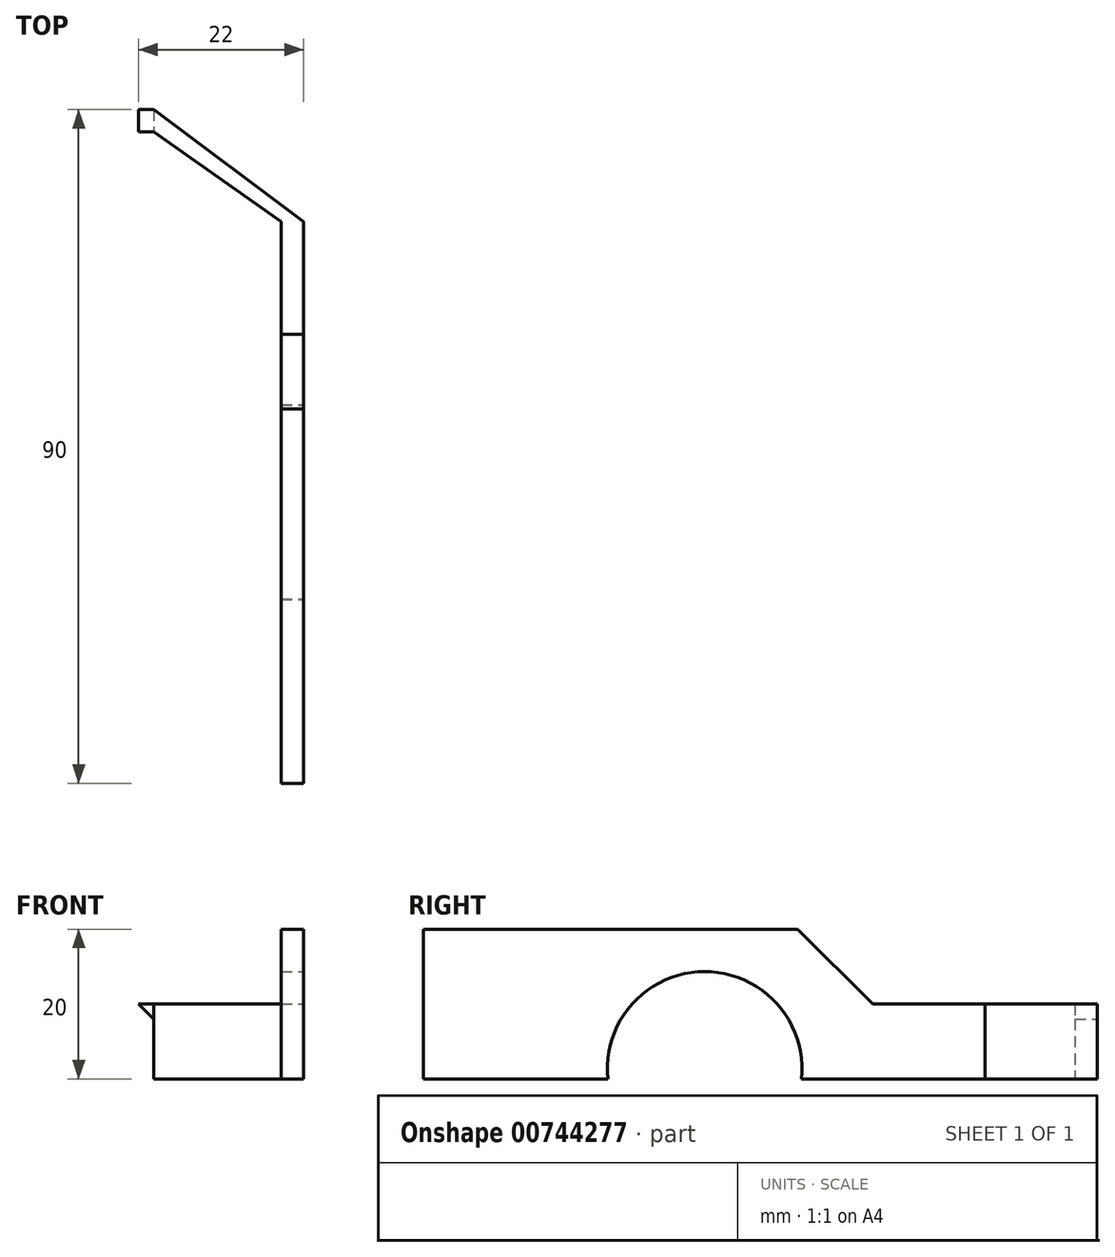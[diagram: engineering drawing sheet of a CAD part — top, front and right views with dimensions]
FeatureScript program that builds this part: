
annotation { "Feature Type Name" : "Feature", "Feature Type Description" : "" }
export const myFeature = defineFeature(function(context is Context, id is Id, definition is map)
    precondition{}
    {
        {
            var Q0;
            Q0=qCreatedBy(makeId("Top.planeOp"),FACE);
            var sketch = newSketch(context, id + "F0", { "sketchPlane" : qUnion([Q0])});
            skLineSegment(sketch, "E0", {"start": v(0, 0) * mm, "end": v(0, -3) * mm});
            skLineSegment(sketch, "E1", {"start": v(0, -3) * mm, "end": v(17, -15) * mm});
            skLineSegment(sketch, "E2", {"start": v(17, -15) * mm, "end": v(17, -90) * mm});
            skLineSegment(sketch, "E3", {"start": v(17, -90) * mm, "end": v(20, -90) * mm});
            skLineSegment(sketch, "E4", {"start": v(20, -90) * mm, "end": v(20, -15) * mm});
            skLineSegment(sketch, "E5", {"start": v(20, -15) * mm, "end": v(0, 0) * mm});
            skSolve(sketch);
        }
        {
            var Q0;
            Q0 = qSketchRegion(id + "F0", true);
            extrude(context, id + "F1", {"entities" : qUnion([Q0]), "depth" : 10 * mm, "offsetDistance" : 25 * mm});
        }
        {
            var Q0;
            Q0=qCreatedBy(makeId("Front.planeOp"),FACE);
            var sketch = newSketch(context, id + "F2", { "sketchPlane" : qUnion([Q0])});
            skLineSegment(sketch, "E6", {"start": v(0, 10) * mm, "end": v(-2, 10) * mm});
            skLineSegment(sketch, "E7", {"start": v(-2, 10) * mm, "end": v(0, 8) * mm});
            skLineSegment(sketch, "E8", {"start": v(0, 8) * mm, "end": v(0, 10) * mm});
            skSolve(sketch);
        }
        {
            var Q0;
            Q0 = qSketchRegion(id + "F2", true);
            extrude(context, id + "F3", {"entities" : qUnion([Q0]), "operationType" : NewBodyOperationType.ADD, "depth" : 3 * mm, "offsetDistance" : 25 * mm});
        }
        {
            var Q0;
            Q0=makeQuery(id+"F3.boolean.opBoolean","MERGE",FACE,{"derivedFrom":[makeQuery(id+"F1.opExtrude","CAP_FACE",FACE,{"disambiguationData":[OSD([sQuery(id+"F0.wireOp",EDGE,"E0"),sQuery(id+"F0.wireOp",EDGE,"E1"),sQuery(id+"F0.wireOp",EDGE,"E2"),sQuery(id+"F0.wireOp",EDGE,"E3"),sQuery(id+"F0.wireOp",EDGE,"E4"),sQuery(id+"F0.wireOp",EDGE,"E5")])],"isStart":false}),makeQuery(id+"F3.opExtrude","SWEPT_FACE",FACE,{"disambiguationData":[OSD([sQuery(id+"F2.wireOp",EDGE,"E6")])]})]});
            var sketch = newSketch(context, id + "F4", { "sketchPlane" : qUnion([Q0])});
            skLineSegment(sketch, "E9.bottom", {"start": v(17, -30) * mm, "end": v(20, -30) * mm});
            skLineSegment(sketch, "E9.top", {"start": v(17, -90) * mm, "end": v(20, -90) * mm});
            skLineSegment(sketch, "E9.left", {"start": v(17, -30) * mm, "end": v(17, -90) * mm});
            skLineSegment(sketch, "E9.right", {"start": v(20, -30) * mm, "end": v(20, -90) * mm});
            skSolve(sketch);
        }
        {
            var Q0;
            Q0 = qSketchRegion(id + "F4", true);
            extrude(context, id + "F5", {"entities" : qUnion([Q0]), "operationType" : NewBodyOperationType.ADD, "depth" : 10 * mm, "offsetDistance" : 25 * mm});
        }
        {
            var Q0;
            Q0=makeQuery(id+"F5.opExtrude","CAP_EDGE",EDGE,{"disambiguationData":[OSD([sQuery(id+"F4.wireOp",EDGE,"E9.bottom")])],"isStart":false});
            chamfer(context, id + "F6", {"entities" : qUnion([Q0]), "width" : 10 * mm, "tangentPropagation" : true});
        }
        {
            var Q0;
            Q0=makeQuery(id+"F5.boolean.opBoolean","MERGE",FACE,{"derivedFrom":[makeQuery(id+"F1.opExtrude","SWEPT_FACE",FACE,{"disambiguationData":[OSD([sQuery(id+"F0.wireOp",EDGE,"E4")])]}),makeQuery(id+"F5.opExtrude","SWEPT_FACE",FACE,{"disambiguationData":[OSD([sQuery(id+"F4.wireOp",EDGE,"E9.right")])]})]});
            var sketch = newSketch(context, id + "F7", { "sketchPlane" : qUnion([Q0])});
            skArc(sketch, "E10", {"start": v(-39.5, 0) * mm, "mid": v(-52.43, 14.33) * mm, "end": v(-65.36, 0) * mm});
            skSolve(sketch);
        }
        {
            var Q0;
            {var subQ0=sQuery(id+"F7.wireOp",EDGE,"E10");Q0=makeQuery(id+"F7.imprint","IMPRINT",FACE,{"disambiguationData":[TD([[makeQuery(id+"F7.imprint","IMPRINT",EDGE,{"derivedFrom":subQ0}),1.0]])]});}
            extrude(context, id + "F8", {"entities" : qUnion([Q0]), "operationType" : NewBodyOperationType.REMOVE, "oppositeDirection" : true, "depth" : 25 * mm, "offsetDistance" : 25 * mm});
        }
    });
